# Revit family: STH8950BR_STH8950BRPTO_STH8950PTO
name_source: partatom
category: Luminárias
units: mm (PartAtom-declared; Revit-internal decimal feet)

## family parameters
Compartilhado = Não
Corte com vazios quando carregada = Não
Cota do conector redondo = Utilizar diâmetro
Fonte luminosa = Não
Hospedeiro = Forro
Manter orientação da anotação = Não
Número OmniClass = 23.80.70.11
Ponto de cálculo do ambiente = Não
Sempre na vertical = Sim
Tipo de parte = Normal
Título OmniClass = Luminaries for Internal Lighting

## types (3) — shared parameters
Altura = 0.11 m
Comentários de tipos = Lâmpada indicada: 1x PAR20 Stella.
Comprimento = 0.11 m
Estrutura Topo = Al - Preto
Fabricante = Stella
Fundo_Branco = Al - Branco
Fundo_Preto = Al - Preto
Largura = 0.11 m
Modelo = Square Ghost PAR20
Potência máxima = 20 W
Tensão Elétrica = 127V-220V
URL = https://stella.com.br
zero-valued in all types: Elevação padrão

## per-type parameters (varying)
| type | Estrutura | Flange Branca | Flange Preta | Fundo Branco | Fundo Preto | Referência | Topo_Preto |
| STH8950PTO - BIVOLT | Al - Preto | Não | Sim | Não | Sim | STH8950PTO | Não |
| STH8950BR/PTO - BIVOLT | Al - Branco | Não | Sim | Não | Sim | STH8950BR/PTO | Sim |
| STH8950BR - BIVOLT | Al - Branco | Sim | Não | Sim | Não | STH8950BR | Não |
